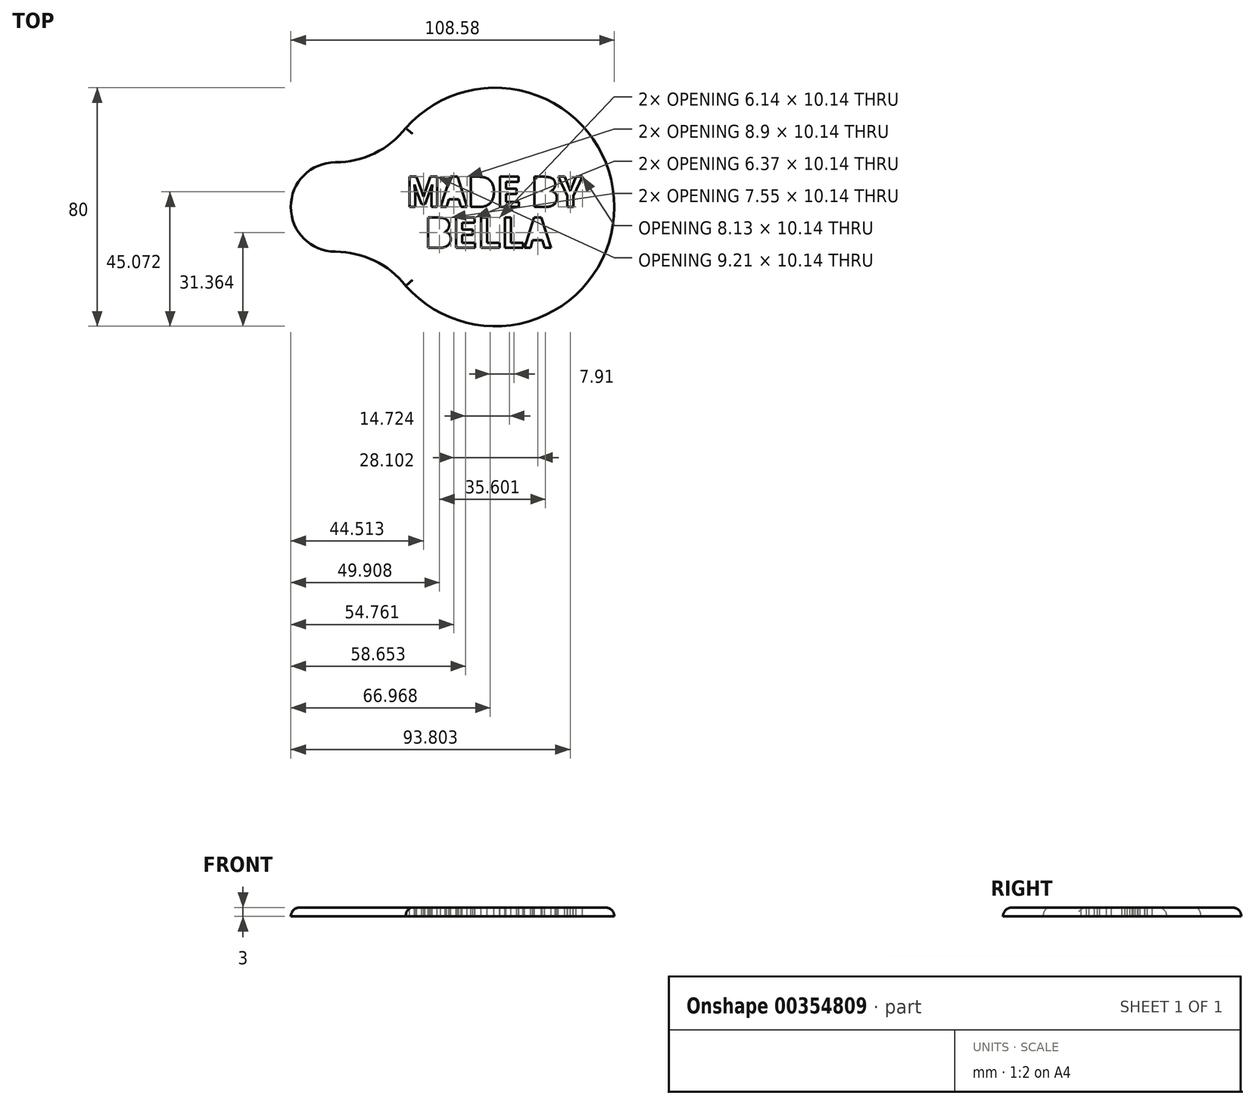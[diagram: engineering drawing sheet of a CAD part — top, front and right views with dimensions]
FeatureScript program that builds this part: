
annotation { "Feature Type Name" : "Feature", "Feature Type Description" : "" }
export const myFeature = defineFeature(function(context is Context, id is Id, definition is map)
    precondition{}
    {
        {
            var Q0;
            Q0=qCreatedBy(makeId("Top.planeOp"),FACE);
            var sketch = newSketch(context, id + "F0", { "sketchPlane" : qUnion([Q0])});
            skLineSegment(sketch, "E0.left", {"start": v(30, 0) * mm, "end": v(30, 0) * mm});
            skLineSegment(sketch, "E0.right", {"start": v(-30, -10) * mm, "end": v(-30, -10) * mm});
            skPoint(sketch, "E0.middle", {"position": v(0, 0) * mm});
            skPoint(sketch, "E1.visualSharp", {"position": v(30, 40) * mm});
            skPoint(sketch, "E2.visualSharp", {"position": v(30, -40) * mm});
            skPoint(sketch, "E3.visualSharp", {"position": v(-30, -40) * mm});
            skLineSegment(sketch, "E4.bottom", {"start": v(-45, 15) * mm, "end": v(-45, 15) * mm});
            skLineSegment(sketch, "E4.top", {"start": v(-45, -15) * mm, "end": v(-45, -15) * mm});
            skPoint(sketch, "E4.middle", {"position": v(-37.5, 0) * mm});
            skArc(sketch, "E5", {"start": v(-45, -15) * mm, "mid": v(-60, 0) * mm, "end": v(-45, 15) * mm});
            skPoint(sketch, "E6.visualSharp", {"position": v(-30, 40) * mm});
            skPoint(sketch, "E7.newPointA", {"position": v(-30, 15) * mm});
            skArc(sketch, "E7.filletArc", {"start": v(-45, 15) * mm, "mid": v(-31.9, 18.01) * mm, "end": v(-21.43, 26.44) * mm});
            skPoint(sketch, "E8.newPointA", {"position": v(-30, -15) * mm});
            skArc(sketch, "E8.filletArc", {"start": v(-21.43, -26.44) * mm, "mid": v(-31.9, -18.01) * mm, "end": v(-45, -15) * mm});
            skArc(sketch, "E9", {"start": v(-21.43, -26.44) * mm, "mid": v(48.58, 0) * mm, "end": v(-21.43, 26.44) * mm});
            skSolve(sketch);
        }
        {
            var Q0;
            Q0 = qSketchRegion(id + "F0", true);
            extrude(context, id + "F1", {"entities" : qUnion([Q0]), "depth" : 3 * mm});
        }
        {
            var Q0;
            Q0=makeQuery(id+"F1.opExtrude","CAP_FACE",FACE,{"disambiguationData":[OSD([sQuery(id+"F0.wireOp",EDGE,"E1.filletArc"),sQuery(id+"F0.wireOp",EDGE,"E2.filletArc"),sQuery(id+"F0.wireOp",EDGE,"E3.filletArc"),sQuery(id+"F0.wireOp",EDGE,"E4.bottom"),sQuery(id+"F0.wireOp",EDGE,"E4.top"),sQuery(id+"F0.wireOp",EDGE,"E5"),sQuery(id+"F0.wireOp",EDGE,"E6.filletArc"),sQuery(id+"F0.wireOp",EDGE,"E7.filletArc"),sQuery(id+"F0.wireOp",EDGE,"E8.filletArc")])],"isStart":false});
            var sketch = newSketch(context, id + "F2", { "sketchPlane" : qUnion([Q0])});
            skText(sketch, "E10", { "text": "MADE BY\n  BELLA", "fontName": "NotoSansCJKsc-Bold.otf"});
            const initialGuessF2  = {"E10": [-0.02134, 0, 1, 0, 0.00987]};
            skSetInitialGuess(sketch, initialGuessF2);
            skSolve(sketch);
        }
        {
            var Q0;
            Q0 = qSketchRegion(id + "F2", true);
            extrude(context, id + "F3", {"entities" : qUnion([Q0]), "operationType" : NewBodyOperationType.REMOVE, "oppositeDirection" : true, "depth" : 25 * mm});
        }
        {
            var Q0;
            Q0=makeQuery(id+"F1.opExtrude","CAP_EDGE",EDGE,{"disambiguationData":[OSD([sQuery(id+"F0.wireOp",EDGE,"E9")])],"isStart":false});
            var Q1;
            Q1=makeQuery(id+"F1.opExtrude","CAP_EDGE",EDGE,{"disambiguationData":[OSD([sQuery(id+"F0.wireOp",EDGE,"E7.filletArc")])],"isStart":false});
            var Q2;
            Q2=makeQuery(id+"F1.opExtrude","CAP_EDGE",EDGE,{"disambiguationData":[OSD([sQuery(id+"F0.wireOp",EDGE,"E5")])],"isStart":false});
            fillet(context, id + "F4", {"entities" : qUnion([Q0, Q1, Q2]), "radius" : 3 * mm, "tangentPropagation" : true, "allowEdgeOverflow" : false});
        }
        {
            var Q0;
            Q0=makeQuery(id+"F2.imprint","IMPRINT",FACE,{"disambiguationData":[TD([[makeQuery(id+"F2.imprint","IMPRINT",EDGE,{"derivedFrom":sQuery(id+"F2.wireOp",EDGE,"E10.sketch_text.stroke-41")}),-1.0]])]});
            var sketch = newSketch(context, id + "F5", { "sketchPlane" : qUnion([Q0])});
            skLineSegment(sketch, "E11.bottom", {"start": v(1.88, 8.81) * mm, "end": v(6.35, 8.81) * mm});
            skLineSegment(sketch, "E11.top", {"start": v(1.88, 1.36) * mm, "end": v(6.35, 1.36) * mm});
            skLineSegment(sketch, "E11.left", {"start": v(1.88, 8.81) * mm, "end": v(1.88, 1.36) * mm});
            skLineSegment(sketch, "E11.right", {"start": v(6.35, 8.81) * mm, "end": v(6.35, 1.36) * mm});
            skSolve(sketch);
        }
        {
            var Q0;
            Q0 = qSketchRegion(id + "F5", true);
            extrude(context, id + "F6", {"entities" : qUnion([Q0]), "operationType" : NewBodyOperationType.REMOVE, "oppositeDirection" : true, "depth" : 25 * mm});
        }
        {
            var Q0;
            Q0=makeQuery(id+"F2.imprint","IMPRINT",FACE,{"disambiguationData":[TD([[makeQuery(id+"F2.imprint","IMPRINT",EDGE,{"derivedFrom":sQuery(id+"F2.wireOp",EDGE,"E10.sketch_text.stroke-22")}),-1.0]])]});
            var sketch = newSketch(context, id + "F7", { "sketchPlane" : qUnion([Q0])});
            skLineSegment(sketch, "E12", {"start": v(-5.33, 9.72) * mm, "end": v(-7.22, 3.74) * mm});
            skLineSegment(sketch, "E13", {"start": v(-7.22, 3.74) * mm, "end": v(-2.65, 3.54) * mm});
            skLineSegment(sketch, "E14", {"start": v(-2.65, 3.54) * mm, "end": v(-5.33, 9.72) * mm});
            skSolve(sketch);
        }
        {
            var Q0;
            Q0 = qSketchRegion(id + "F7", true);
            extrude(context, id + "F8", {"entities" : qUnion([Q0]), "operationType" : NewBodyOperationType.REMOVE, "oppositeDirection" : true, "depth" : 25 * mm});
        }
        {
            var Q0;
            Q0=makeQuery(id+"F2.imprint","IMPRINT",FACE,{"disambiguationData":[TD([[makeQuery(id+"F2.imprint","IMPRINT",EDGE,{"derivedFrom":sQuery(id+"F2.wireOp",EDGE,"E10.sketch_text.stroke-71")}),-1.0]])]});
            var sketch = newSketch(context, id + "F9", { "sketchPlane" : qUnion([Q0])});
            skLineSegment(sketch, "E15", {"start": v(22.64, 5.19) * mm, "end": v(23.04, 0.99) * mm});
            skLineSegment(sketch, "E16", {"start": v(23.04, 0.99) * mm, "end": v(28.32, 1.48) * mm});
            skLineSegment(sketch, "E17", {"start": v(28.32, 1.48) * mm, "end": v(27.81, 4.6) * mm});
            skLineSegment(sketch, "E18", {"start": v(27.81, 4.6) * mm, "end": v(22.64, 5.19) * mm});
            skSolve(sketch);
        }
        {
            var Q0;
            Q0 = qSketchRegion(id + "F9", true);
            extrude(context, id + "F10", {"entities" : qUnion([Q0]), "operationType" : NewBodyOperationType.REMOVE, "oppositeDirection" : true, "depth" : 25 * mm});
        }
        {
            var Q0;
            Q0=makeQuery(id+"F2.imprint","IMPRINT",FACE,{"disambiguationData":[TD([[makeQuery(id+"F2.imprint","IMPRINT",EDGE,{"derivedFrom":sQuery(id+"F2.wireOp",EDGE,"E10.sketch_text.stroke-66")}),-1.0]])]});
            var sketch = newSketch(context, id + "F11", { "sketchPlane" : qUnion([Q0])});
            skLineSegment(sketch, "E19", {"start": v(22.82, 9.24) * mm, "end": v(22.82, 5.83) * mm});
            skLineSegment(sketch, "E20", {"start": v(22.82, 5.83) * mm, "end": v(27.2, 5.83) * mm});
            skLineSegment(sketch, "E21", {"start": v(27.2, 5.83) * mm, "end": v(27.2, 9.06) * mm});
            skLineSegment(sketch, "E22", {"start": v(27.2, 9.06) * mm, "end": v(22.82, 9.24) * mm});
            skSolve(sketch);
        }
        {
            var Q0;
            Q0 = qSketchRegion(id + "F11", true);
            extrude(context, id + "F12", {"entities" : qUnion([Q0]), "operationType" : NewBodyOperationType.REMOVE, "oppositeDirection" : true, "depth" : 25 * mm});
        }
        {
            var Q0;
            Q0=makeQuery(id+"F2.imprint","IMPRINT",FACE,{"disambiguationData":[TD([[makeQuery(id+"F2.imprint","IMPRINT",EDGE,{"derivedFrom":sQuery(id+"F2.wireOp",EDGE,"E10.sketch_text.stroke-101")}),-1.0]])]});
            var sketch = newSketch(context, id + "F13", { "sketchPlane" : qUnion([Q0])});
            skLineSegment(sketch, "E23", {"start": v(-12.72, -8.5) * mm, "end": v(-12.72, -12.72) * mm});
            skLineSegment(sketch, "E24", {"start": v(-12.72, -12.72) * mm, "end": v(-7.22, -12.26) * mm});
            skLineSegment(sketch, "E25", {"start": v(-7.22, -12.26) * mm, "end": v(-7.46, -9.44) * mm});
            skLineSegment(sketch, "E26", {"start": v(-7.46, -9.44) * mm, "end": v(-12.72, -8.5) * mm});
            skSolve(sketch);
        }
        {
            var Q0;
            Q0 = qSketchRegion(id + "F13", true);
            extrude(context, id + "F14", {"entities" : qUnion([Q0]), "operationType" : NewBodyOperationType.REMOVE, "oppositeDirection" : true, "depth" : 25 * mm});
        }
        {
            var Q0;
            Q0=makeQuery(id+"F2.imprint","IMPRINT",FACE,{"disambiguationData":[TD([[makeQuery(id+"F2.imprint","IMPRINT",EDGE,{"derivedFrom":sQuery(id+"F2.wireOp",EDGE,"E10.sketch_text.stroke-96")}),-1.0]])]});
            var sketch = newSketch(context, id + "F15", { "sketchPlane" : qUnion([Q0])});
            skLineSegment(sketch, "E27", {"start": v(-12.97, -4.32) * mm, "end": v(-12.55, -8.3) * mm});
            skLineSegment(sketch, "E28", {"start": v(-12.55, -8.3) * mm, "end": v(-10.19, -8.61) * mm});
            skLineSegment(sketch, "E29", {"start": v(-10.19, -8.61) * mm, "end": v(-9.54, -7.97) * mm});
            skLineSegment(sketch, "E30", {"start": v(-9.54, -7.97) * mm, "end": v(-8.86, -8.65) * mm});
            skLineSegment(sketch, "E31", {"start": v(-8.86, -8.65) * mm, "end": v(-8.18, -5.29) * mm});
            skLineSegment(sketch, "E32", {"start": v(-8.18, -5.29) * mm, "end": v(-12.33, -3.79) * mm});
            skLineSegment(sketch, "E33", {"start": v(-12.33, -3.79) * mm, "end": v(-12.97, -4.32) * mm});
            skSolve(sketch);
        }
        {
            var Q0;
            Q0 = qSketchRegion(id + "F15", true);
            extrude(context, id + "F16", {"entities" : qUnion([Q0]), "operationType" : NewBodyOperationType.REMOVE, "oppositeDirection" : true, "depth" : 25 * mm});
        }
        {
            var Q0;
            Q0=makeQuery(id+"F2.imprint","IMPRINT",FACE,{"disambiguationData":[TD([[makeQuery(id+"F2.imprint","IMPRINT",EDGE,{"derivedFrom":sQuery(id+"F2.wireOp",EDGE,"E10.sketch_text.stroke-130")}),-1.0]])]});
            var sketch = newSketch(context, id + "F17", { "sketchPlane" : qUnion([Q0])});
            skLineSegment(sketch, "E34", {"start": v(22.38, -3.65) * mm, "end": v(26.56, -11.68) * mm});
            skLineSegment(sketch, "E35", {"start": v(26.56, -11.68) * mm, "end": v(21.52, -9.63) * mm});
            skLineSegment(sketch, "E36", {"start": v(21.52, -9.63) * mm, "end": v(22.38, -3.65) * mm});
            skSolve(sketch);
        }
        {
            var Q0;
            Q0 = qSketchRegion(id + "F17", true);
            extrude(context, id + "F18", {"entities" : qUnion([Q0]), "operationType" : NewBodyOperationType.REMOVE, "oppositeDirection" : true, "depth" : 25 * mm});
        }
    });
